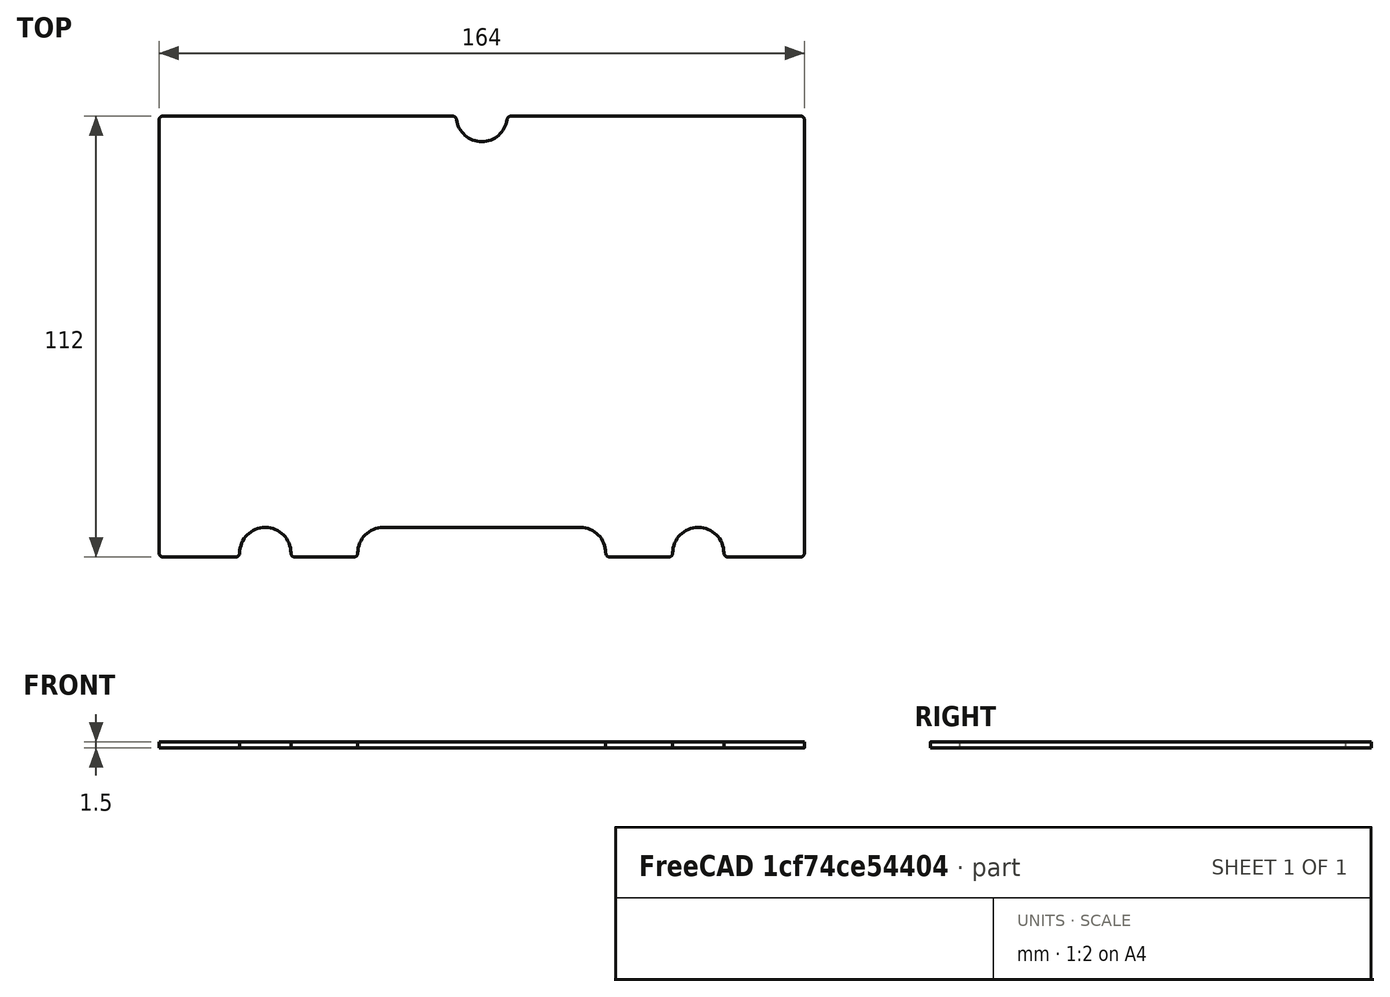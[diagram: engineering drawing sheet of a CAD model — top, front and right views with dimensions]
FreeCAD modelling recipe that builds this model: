
FCSTD DOCUMENT  (FreeCAD 0.22R35391 (Git))
Label: heater
License: All rights reserved
LicenseURL: http://en.wikipedia.org/wiki/All_rights_reserved
objects: Sketcher::SketchObject×1, Part::Extrusion×1
note: 2 computed .brp shape members not serialized (recipe doc carries the construction recipe); baked Part::Feature solids carry a one-line shape summary decoded from their .brp

FEATURE [Sketcher::SketchObject] Sketch
  FullyConstrained = false
  sketch-geometry (28):
    g0: LineSegment StartX=82 StartY=-55 StartZ=0 EndX=82 EndY=55 EndZ=0
    g1: LineSegment StartX=81 StartY=56 StartZ=0 EndX=7.43303 EndY=56 EndZ=0
    g2: LineSegment StartX=32.5 StartY=-56 StartZ=0 EndX=47.5 EndY=-56 EndZ=0
    g3: LineSegment StartX=62.5 StartY=-56 StartZ=0 EndX=81 EndY=-56 EndZ=0
    g4: ArcOfCircle CenterX=55 CenterY=-55 CenterZ=0 NormalX=0 NormalY=0 NormalZ=1 AngleXU=0 Radius=6.5 StartAngle=6e-16 EndAngle=3.14159
    g5: ArcOfCircle CenterX=47.5 CenterY=-55 CenterZ=0 NormalX=0 NormalY=0 NormalZ=1 AngleXU=0 Radius=1 StartAngle=4.71239 EndAngle=6.28319
    g6: ArcOfCircle CenterX=62.5 CenterY=-55 CenterZ=0 NormalX=0 NormalY=0 NormalZ=1 AngleXU=0 Radius=1 StartAngle=3.14159 EndAngle=4.71239
    g7: ArcOfCircle CenterX=81 CenterY=-55 CenterZ=0 NormalX=0 NormalY=0 NormalZ=1 AngleXU=0 Radius=1 StartAngle=4.71239 EndAngle=6.28319
    g8: ArcOfCircle CenterX=81 CenterY=55 CenterZ=0 NormalX=0 NormalY=0 NormalZ=1 AngleXU=0 Radius=1 StartAngle=-2.7e-15 EndAngle=1.5708
    g9: LineSegment StartX=25 StartY=-48.5 StartZ=0 EndX=0 EndY=-48.5 EndZ=0
    g10: ArcOfCircle CenterX=0 CenterY=56 CenterZ=0 NormalX=0 NormalY=0 NormalZ=1 AngleXU=0 Radius=6.5 StartAngle=4.71239 EndAngle=6.14945
    g11: ArcOfCircle CenterX=7.43303 CenterY=55 CenterZ=0 NormalX=0 NormalY=0 NormalZ=1 AngleXU=0 Radius=1 StartAngle=1.5708 EndAngle=3.00786
    g12: ArcOfCircle CenterX=25 CenterY=-55 CenterZ=0 NormalX=0 NormalY=0 NormalZ=1 AngleXU=0 Radius=6.5 StartAngle=2e-16 EndAngle=1.5708
    g13: ArcOfCircle CenterX=32.5 CenterY=-55 CenterZ=0 NormalX=0 NormalY=0 NormalZ=1 AngleXU=0 Radius=1 StartAngle=3.14159 EndAngle=4.71239
    g14: LineSegment StartX=-82 StartY=-55 StartZ=0 EndX=-82 EndY=55 EndZ=0
    g15: LineSegment StartX=-81 StartY=56 StartZ=0 EndX=-7.43303 EndY=56 EndZ=0
    g16: LineSegment StartX=-32.5 StartY=-56 StartZ=0 EndX=-47.5 EndY=-56 EndZ=0
    g17: LineSegment StartX=-62.5 StartY=-56 StartZ=0 EndX=-81 EndY=-56 EndZ=0
    g18: ArcOfCircle CenterX=-55 CenterY=-55 CenterZ=0 NormalX=0 NormalY=0 NormalZ=1 AngleXU=0 Radius=6.5 StartAngle=0 EndAngle=3.14159
    g19: ArcOfCircle CenterX=-47.5 CenterY=-55 CenterZ=0 NormalX=0 NormalY=0 NormalZ=1 AngleXU=0 Radius=1 StartAngle=3.14159 EndAngle=4.71239
    g20: ArcOfCircle CenterX=-62.5 CenterY=-55 CenterZ=0 NormalX=0 NormalY=0 NormalZ=1 AngleXU=0 Radius=1 StartAngle=4.71239 EndAngle=6.28319
    g21: ArcOfCircle CenterX=-81 CenterY=-55 CenterZ=0 NormalX=0 NormalY=0 NormalZ=1 AngleXU=0 Radius=1 StartAngle=3.14159 EndAngle=4.71239
    g22: ArcOfCircle CenterX=-81 CenterY=55 CenterZ=0 NormalX=0 NormalY=0 NormalZ=1 AngleXU=0 Radius=1 StartAngle=1.5708 EndAngle=3.14159
    g23: LineSegment StartX=-25 StartY=-48.5 StartZ=0 EndX=0 EndY=-48.5 EndZ=0
    g24: ArcOfCircle CenterX=0 CenterY=56 CenterZ=0 NormalX=0 NormalY=0 NormalZ=1 AngleXU=0 Radius=6.5 StartAngle=3.27532 EndAngle=4.71239
    g25: ArcOfCircle CenterX=-7.43303 CenterY=55 CenterZ=0 NormalX=0 NormalY=0 NormalZ=1 AngleXU=0 Radius=1 StartAngle=0.133732 EndAngle=1.5708
    g26: ArcOfCircle CenterX=-25 CenterY=-55 CenterZ=0 NormalX=0 NormalY=0 NormalZ=1 AngleXU=0 Radius=6.5 StartAngle=1.5708 EndAngle=3.14159
    g27: ArcOfCircle CenterX=-32.5 CenterY=-55 CenterZ=0 NormalX=0 NormalY=0 NormalZ=1 AngleXU=0 Radius=1 StartAngle=4.71239 EndAngle=6.28319
  constraints (69):
    c: Horizontal(g3)
    c: Horizontal(g2)
    c: Horizontal(g1)
    c: Tangent(g2,g5) = -1.5708
    c: Radius(g5) = 1
    c: Tangent(g3,g6) = -1.5708
    c: Equal(g6,g5)
    c: Tangent(g3,g7) = -1.5708
    c: Tangent(g0,g7) = -1.5708
    c: Equal(g6,g7)
    c: Tangent(g1,g8) = -1.5708
    c: Tangent(g0,g8) = -1.5708
    c: Equal(g7,g8)
    c: PointOnObject(g9,g-2)
    c: Horizontal(g9)
    c: Tangent(g1,g11) = -1.5708
    c: PointOnObject(g10,g-2)
    c: Equal(g13,g5)
    c: Equal(g13,g11)
    c: Radius(g10) = 6.5
    c: DistanceY(g3,g1) = 112
    c: Symmetric(g1,g3,g-1)
    c: DistanceX(g10,g0) = 82
    c: Tangent(g10,g11) = 1.5708
    c: Perpendicular(g10,g-2)
    c: Perpendicular(g10,g1)
    c: Equal(g4,g12)
    c: Diameter(g4) = 13
    c: Tangent(g9,g12) = -1.5708
    c: Tangent(g4,g5) = 1.5708
    c: Tangent(g4,g6) = 1.5708
    c: Horizontal(g3,g2)
    c: Angle(g4) = 3.14159
    c: Angle(g12) = 1.5708
    c: Tangent(g2,g13) = -1.5708
    c: Tangent(g13,g12) = 1.5708
    c: Distance(g12,g-2) = 25
    c: DistanceX(g-1,g4) = 55
    c: Horizontal(g17)
    c: Horizontal(g16)
    c: Horizontal(g15)
    c: Tangent(g16,g19) = 1.5708
    c: Radius(g19) = 1
    c: Tangent(g17,g20) = 1.5708
    c: Equal(g20,g19)
    c: Tangent(g17,g21) = 1.5708
    c: Tangent(g14,g21) = 1.5708
    c: Equal(g20,g21)
    c: Tangent(g15,g22) = 1.5708
    c: Tangent(g14,g22) = 1.5708
    c: Equal(g21,g22)
    c: Horizontal(g23)
    c: Tangent(g15,g25) = 1.5708
    c: Equal(g27,g19)
    c: Equal(g27,g25)
    c: Radius(g24) = 6.5
    c: Tangent(g24,g25) = 1.5708
    c: Perpendicular(g24,g15)
    c: Equal(g18,g26)
    c: Diameter(g18) = 13
    c: Tangent(g23,g26) = 1.5708
    c: Tangent(g18,g19) = 1.5708
    c: Tangent(g18,g20) = 1.5708
    c: Angle(g18) = 3.14159
    c: Angle(g26) = 1.5708
    c: Tangent(g16,g27) = 1.5708
    c: Tangent(g27,g26) = 1.5708
    c: Coincident(g10,g24)
    c: Coincident(g9,g23)
FEATURE [Part::Extrusion] Extrude
  Base = -> Sketch
  Dir = (0,0,1)
  DirMode = 2
  FaceMakerClass = Part::FaceMakerBullseye
  LengthFwd = 1.5
  LengthRev = 0
  Solid = true
  Symmetric = false
